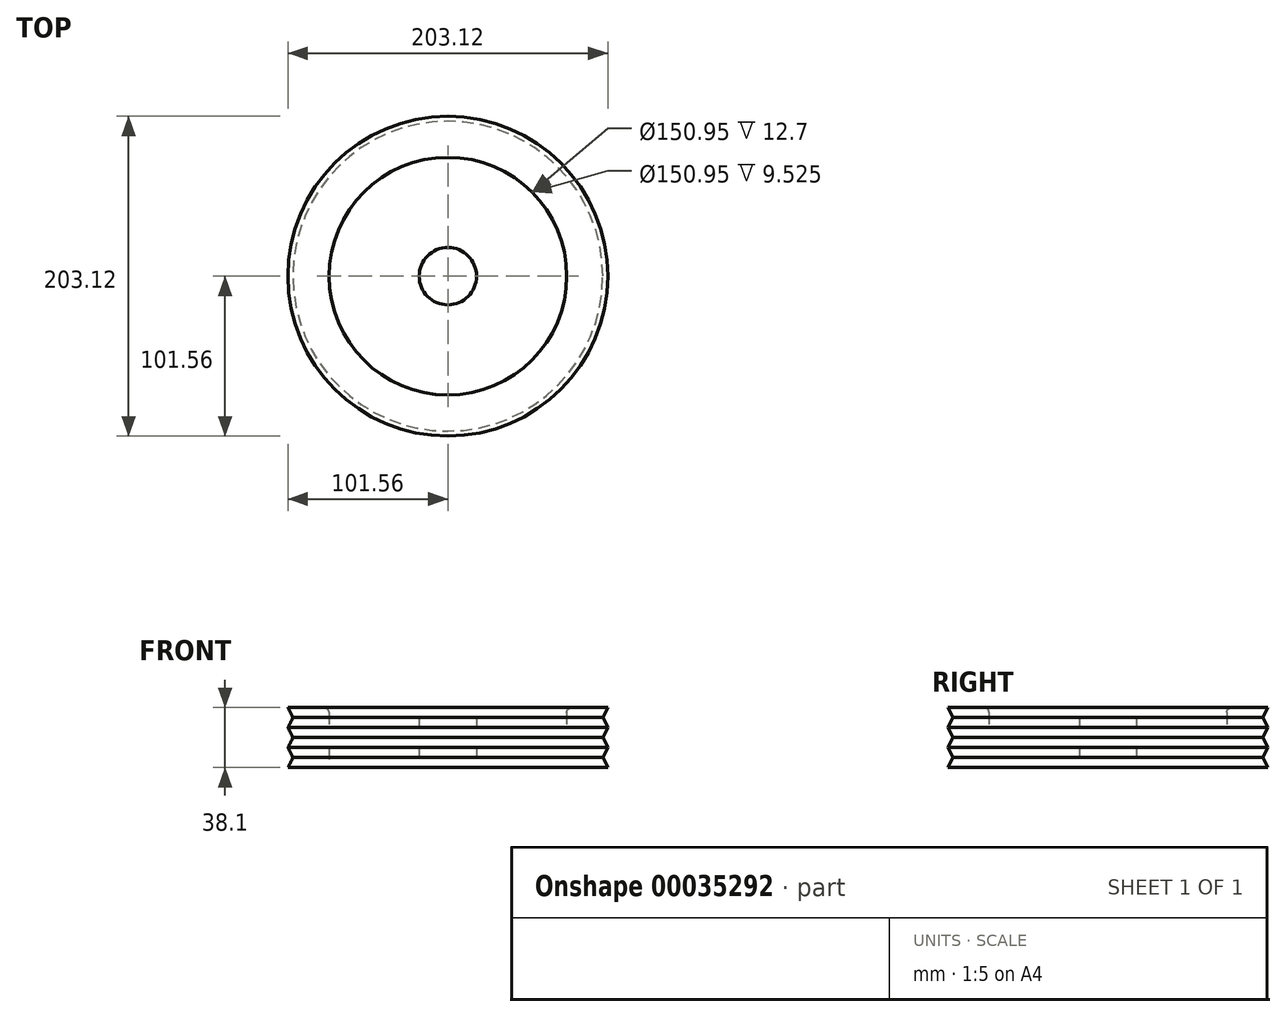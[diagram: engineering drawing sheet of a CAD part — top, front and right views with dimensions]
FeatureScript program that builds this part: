
annotation { "Feature Type Name" : "Feature", "Feature Type Description" : "" }
export const myFeature = defineFeature(function(context is Context, id is Id, definition is map)
    precondition{}
    {
        {
            var Q0;
            Q0=qCreatedBy(makeId("Front.planeOp"),FACE);
            var sketch = newSketch(context, id + "F0", { "sketchPlane" : qUnion([Q0])});
            skLineSegment(sketch, "E0", {"start": v(0, 0) * mm, "end": v(0, 13.43) * mm});
            skLineSegment(sketch, "E1", {"start": v(0, 13.43) * mm, "end": v(18.21, 13.43) * mm});
            skLineSegment(sketch, "E2", {"start": v(18.21, 13.43) * mm, "end": v(18.21, 6.64) * mm});
            skLineSegment(sketch, "E3", {"start": v(18.21, 6.64) * mm, "end": v(75.47, 6.64) * mm});
            skLineSegment(sketch, "E4", {"start": v(75.47, 6.64) * mm, "end": v(75.47, 19.34) * mm});
            skLineSegment(sketch, "E5", {"start": v(75.47, 19.34) * mm, "end": v(101.56, 19.34) * mm});
            skLineSegment(sketch, "E6", {"start": v(101.56, 19.34) * mm, "end": v(98.38, 12.99) * mm});
            skLineSegment(sketch, "E7", {"start": v(101.56, 19.34) * mm, "end": v(101.56, -40.69) * mm, "construction": true});
            skLineSegment(sketch, "E8", {"start": v(98.38, 12.99) * mm, "end": v(101.56, 6.64) * mm});
            skLineSegment(sketch, "E9", {"start": v(101.56, 6.64) * mm, "end": v(98.38, 0.29) * mm});
            skLineSegment(sketch, "E10", {"start": v(98.38, 0.29) * mm, "end": v(101.56, -6.06) * mm});
            skLineSegment(sketch, "E11", {"start": v(101.56, -6.06) * mm, "end": v(98.38, -12.41) * mm});
            skLineSegment(sketch, "E12", {"start": v(98.38, -12.41) * mm, "end": v(101.56, -18.76) * mm});
            skLineSegment(sketch, "E13", {"start": v(101.56, -18.76) * mm, "end": v(75.47, -18.76) * mm});
            skLineSegment(sketch, "E14", {"start": v(75.47, -18.76) * mm, "end": v(75.47, 6.64) * mm, "construction": true});
            skLineSegment(sketch, "E15", {"start": v(98.38, 12.99) * mm, "end": v(98.38, -12.41) * mm, "construction": true});
            skLineSegment(sketch, "E16", {"start": v(75.47, -18.76) * mm, "end": v(75.47, -6.06) * mm});
            skLineSegment(sketch, "E17", {"start": v(75.47, -6.06) * mm, "end": v(18.21, -6.06) * mm});
            skLineSegment(sketch, "E18", {"start": v(18.21, -6.06) * mm, "end": v(18.21, -12.74) * mm});
            skLineSegment(sketch, "E19", {"start": v(18.21, -12.74) * mm, "end": v(0, -12.74) * mm});
            skLineSegment(sketch, "E20", {"start": v(0, -12.74) * mm, "end": v(0, 0) * mm});
            skLineSegment(sketch, "E21", {"start": v(18.21, 6.64) * mm, "end": v(18.21, -6.06) * mm, "construction": true});
            skSolve(sketch);
        }
        {
            var Q0;
            Q0=makeQuery(id+"F0.imprint","IMPRINT",FACE,{"disambiguationData":[TD([[makeQuery(id+"F0.imprint","IMPRINT",EDGE,{"derivedFrom":sQuery(id+"F0.wireOp",EDGE,"E0")}),-1.0]])]});
            var Q1;
            Q1=sQuery(id+"F0.wireOp",EDGE,"E0");
            revolve(context, id + "F1", {"entities" : qUnion([Q0]), "axis" : qUnion([Q1]), "revolveType" : RevolveType.FULL});
        }
        {
            var Q0;
            Q0=makeQuery(id+"F1.opRevolve","SWEPT_EDGE",EDGE,{"disambiguationData":[OSD([sQuery(id+"F0.wireOp",EDGE,"E4"),sQuery(id+"F0.wireOp",EDGE,"E5")])]});
            fillet(context, id + "F2", {"entities" : qUnion([Q0]), "radius" : 3.17 * mm, "tangentPropagation" : true, "allowEdgeOverflow" : false});
        }
    });
